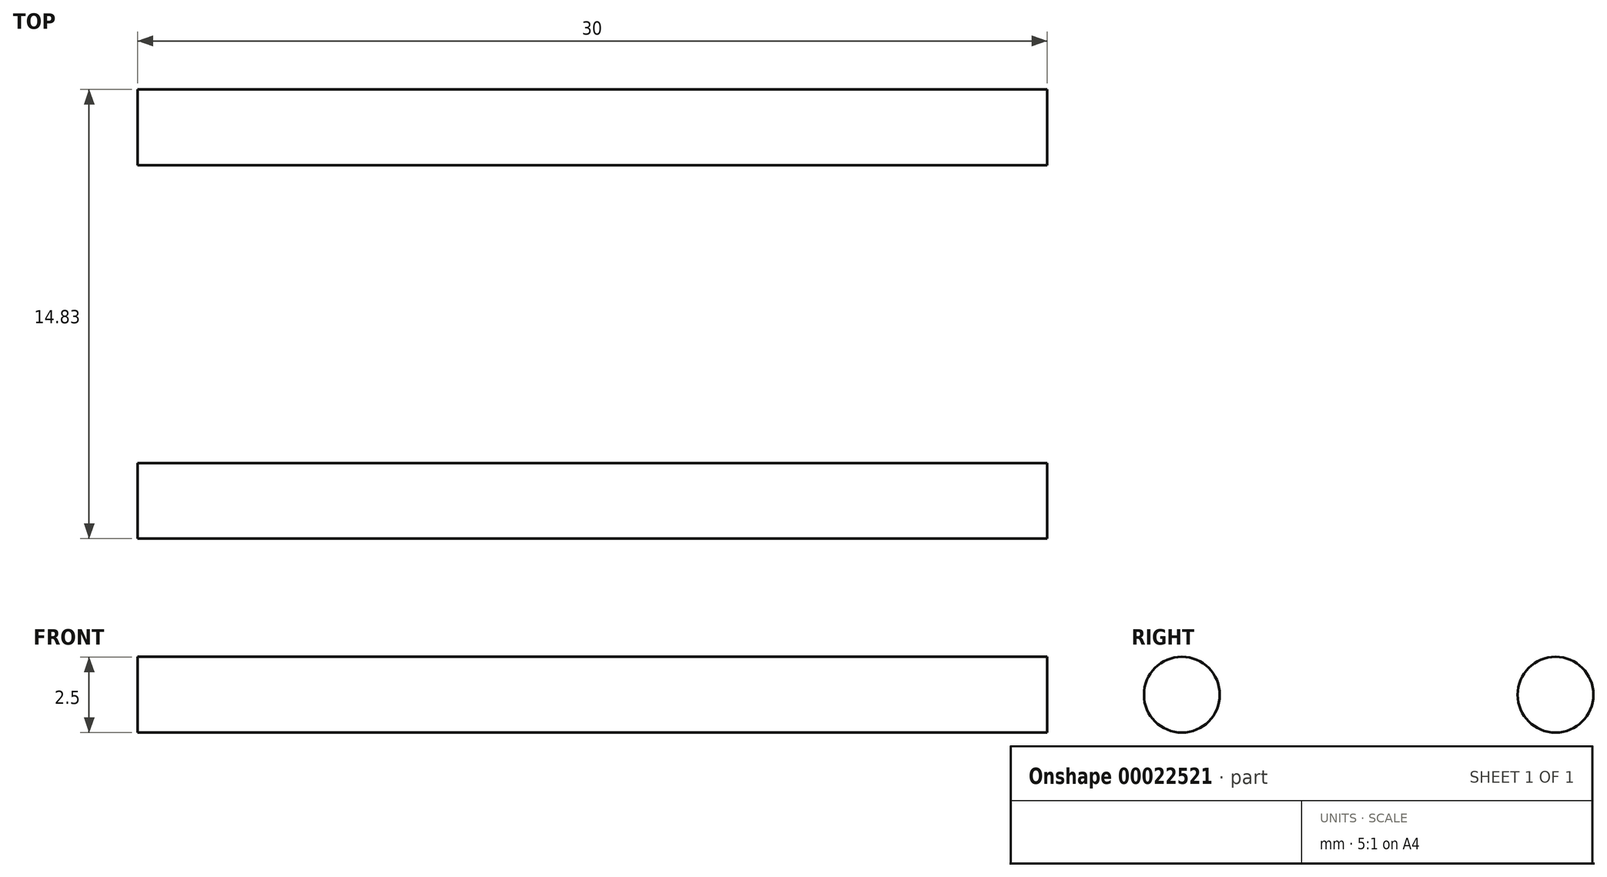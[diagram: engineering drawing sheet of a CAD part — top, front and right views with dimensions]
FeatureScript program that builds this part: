
annotation { "Feature Type Name" : "Feature", "Feature Type Description" : "" }
export const myFeature = defineFeature(function(context is Context, id is Id, definition is map)
    precondition{}
    {
        {
            var Q0;
            Q0=qCreatedBy(makeId("Right.planeOp"),FACE);
            var sketch = newSketch(context, id + "F0", { "sketchPlane" : qUnion([Q0])});
            skCircle(sketch, "E0", {"center": v(-43.1, 35.97) * mm, "radius": 1.25 * mm});
            skCircle(sketch, "E1", {"center": v(-30.78, 35.97) * mm, "radius": 1.25 * mm});
            skSolve(sketch);
        }
        {
            var Q0;
            Q0=makeQuery(id+"F0.imprint","IMPRINT",FACE,{"disambiguationData":[TD([[makeQuery(id+"F0.imprint","IMPRINT",EDGE,{"derivedFrom":sQuery(id+"F0.wireOp",EDGE,"E0")}),1.0]])]});
            var Q1;
            Q1=makeQuery(id+"F0.imprint","IMPRINT",FACE,{"disambiguationData":[TD([[makeQuery(id+"F0.imprint","IMPRINT",EDGE,{"derivedFrom":sQuery(id+"F0.wireOp",EDGE,"E1")}),1.0]])]});
            extrude(context, id + "F1", {"entities" : qUnion([Q0, Q1]), "depth" : 30 * mm});
        }
    });
